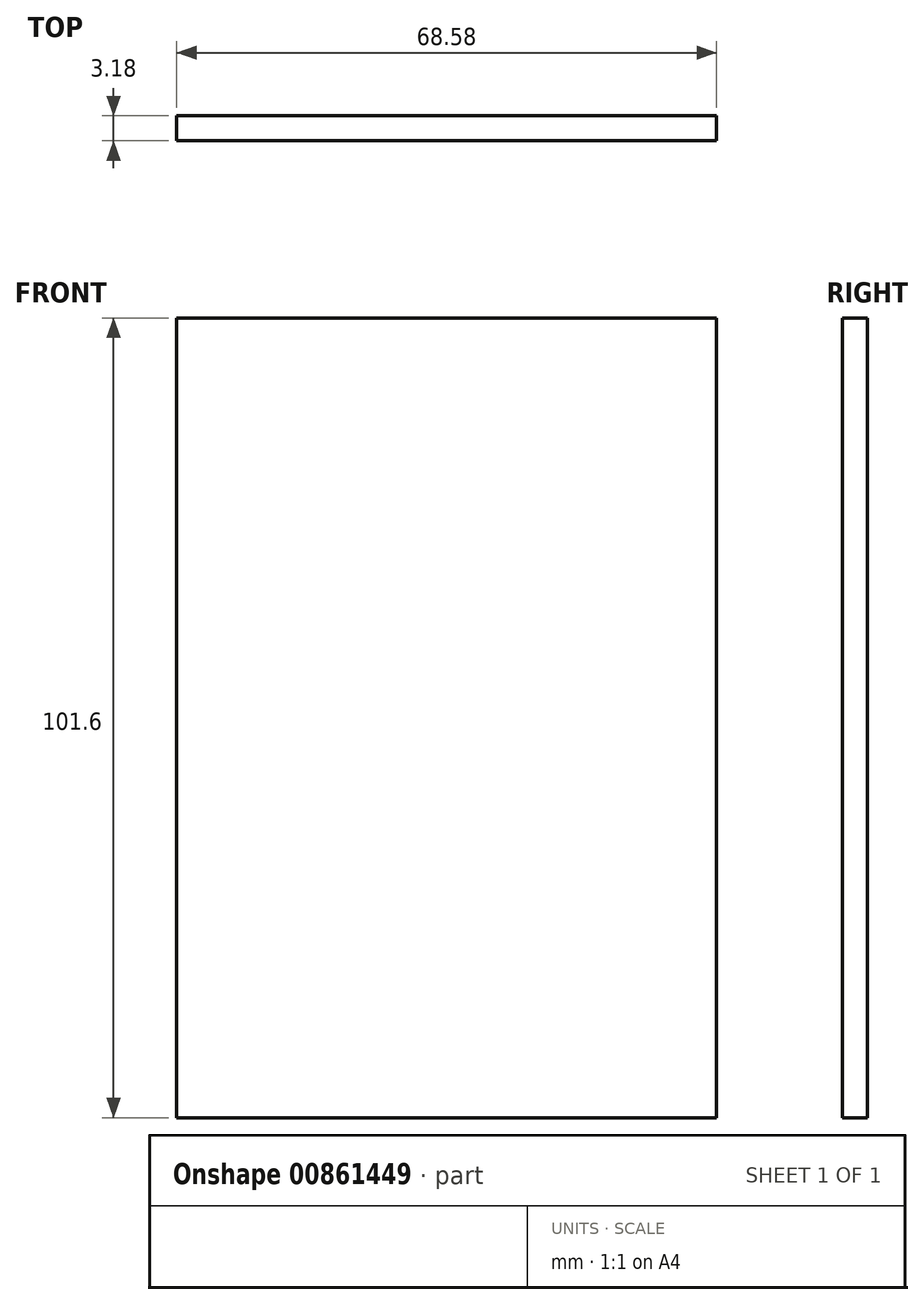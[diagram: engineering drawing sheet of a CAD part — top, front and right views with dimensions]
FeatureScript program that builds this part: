
annotation { "Feature Type Name" : "Feature", "Feature Type Description" : "" }
export const myFeature = defineFeature(function(context is Context, id is Id, definition is map)
    precondition{}
    {
        {
            var Q0;
            Q0=qCreatedBy(makeId("Front.planeOp"),FACE);
            var sketch = newSketch(context, id + "F0", { "sketchPlane" : qUnion([Q0])});
            skLineSegment(sketch, "E0.bottom", {"start": v(34.3, -50.8) * mm, "end": v(-34.3, -50.8) * mm});
            skLineSegment(sketch, "E0.top", {"start": v(34.3, 50.8) * mm, "end": v(-34.3, 50.8) * mm});
            skLineSegment(sketch, "E0.left", {"start": v(34.3, -50.8) * mm, "end": v(34.29, 50.8) * mm});
            skLineSegment(sketch, "E0.right", {"start": v(-34.3, -50.8) * mm, "end": v(-34.3, 50.8) * mm});
            skPoint(sketch, "E0.middle", {"position": v(0, 0) * mm});
            skSolve(sketch);
        }
        {
            var Q0;
            Q0 = qSketchRegion(id + "F0", true);
            extrude(context, id + "F1", {"entities" : qUnion([Q0]), "depth" : 3.17 * mm, "offsetDistance" : 25.4 * mm, "symmetric" : true});
        }
    });
